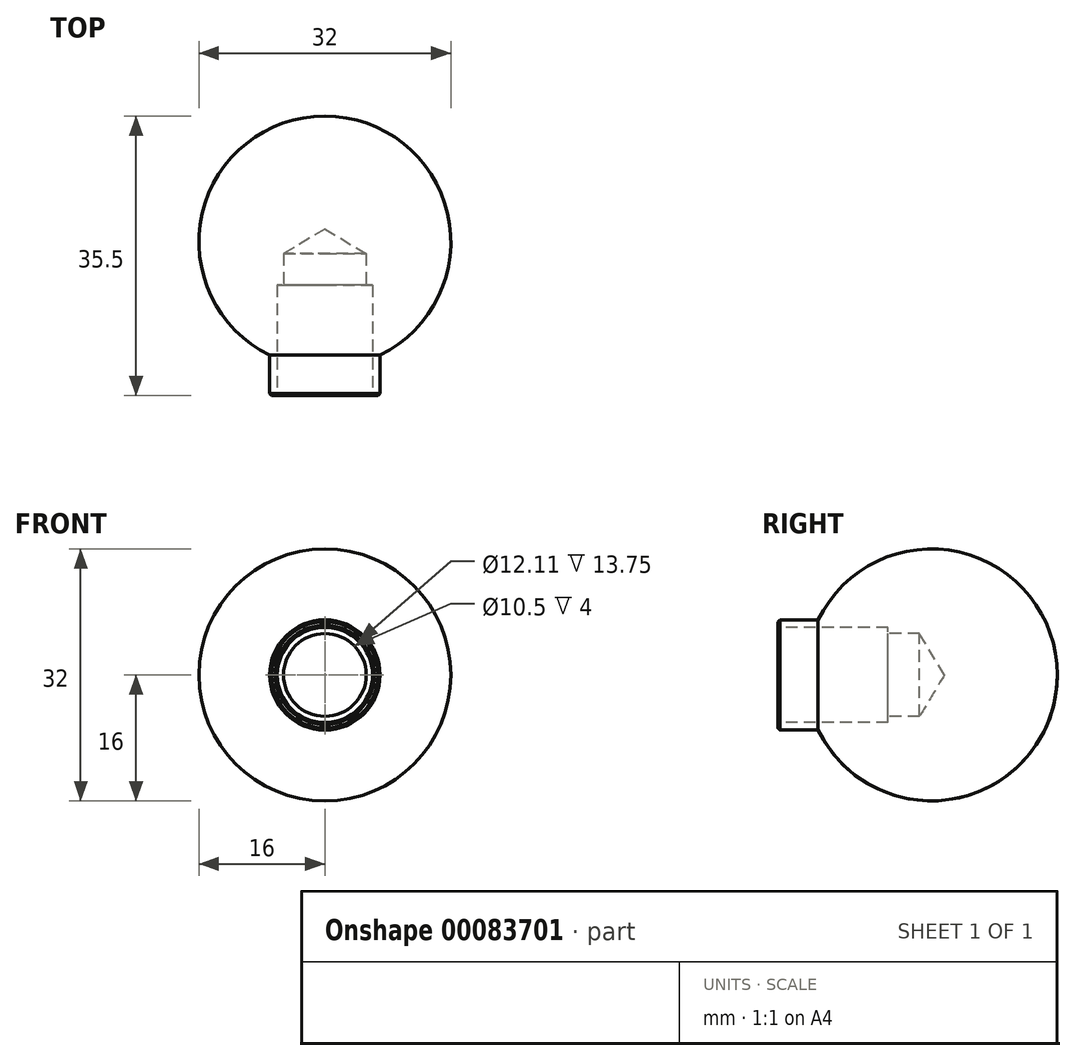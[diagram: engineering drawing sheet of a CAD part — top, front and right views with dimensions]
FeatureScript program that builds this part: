
annotation { "Feature Type Name" : "Feature", "Feature Type Description" : "" }
export const myFeature = defineFeature(function(context is Context, id is Id, definition is map)
    precondition{}
    {
        {
            var Q0;
            Q0=qCreatedBy(makeId("Right.planeOp"),FACE);
            var sketch = newSketch(context, id + "F0", { "sketchPlane" : qUnion([Q0])});
            skArc(sketch, "E0", {"start": v(-14.39, 7) * mm, "mid": v(3.6, 15.6) * mm, "end": v(16, 0) * mm});
            skLineSegment(sketch, "E1", {"start": v(-16, 0) * mm, "end": v(16, 0) * mm});
            skLineSegment(sketch, "E2.left", {"start": v(-16, 0) * mm, "end": v(-16, 0) * mm});
            skLineSegment(sketch, "E3.bottom", {"start": v(-16, 0) * mm, "end": v(-19.5, 0) * mm});
            skLineSegment(sketch, "E3.top", {"start": v(-16, 7) * mm, "end": v(-19.5, 7) * mm});
            skLineSegment(sketch, "E3.right", {"start": v(-19.5, 0) * mm, "end": v(-19.5, 7) * mm});
            skLineSegment(sketch, "E4", {"start": v(-16, 7) * mm, "end": v(-14.39, 7) * mm});
            skSolve(sketch);
        }
        {
            var Q0;
            Q0=qSketchRegion(id+"F0",true);
            var Q1;
            Q1=sQuery(id+"F0.wireOp",EDGE,"E1");
            revolve(context, id + "F1", {"entities" : qUnion([Q0]), "axis" : qUnion([Q1]), "revolveType" : RevolveType.FULL});
        }
        {
            var Q0;
            Q0=makeQuery(id+"F1.opRevolve","SWEPT_FACE",FACE,{"disambiguationData":[OSD([sQuery(id+"F0.wireOp",EDGE,"E3.right")])]});
            var sketch = newSketch(context, id + "F2", { "sketchPlane" : qUnion([Q0])});
            skPoint(sketch, "E5", {"position": v(0, 0) * mm});
            skSolve(sketch);
        }
        {
            var Q0;
            Q0=sQuery(id+"F2.wireOp",VERTEX,"E5");
            var Q1;
            Q1=makeQuery(id+"F1.opRevolve","SWEPT_BODY",BODY,{"disambiguationData":[OSD([sQuery(id+"F0.wireOp",EDGE,"E0"),sQuery(id+"F0.wireOp",EDGE,"E1"),sQuery(id+"F0.wireOp",EDGE,"E3.bottom"),sQuery(id+"F0.wireOp",EDGE,"E3.top"),sQuery(id+"F0.wireOp",EDGE,"E3.right"),sQuery(id+"F0.wireOp",EDGE,"E4")])]});
            hole(context, id + "F3", {"style" : HoleStyle.SIMPLE, "holeDiameter" : 10.5 * mm, "endStyle" : HoleEndStyle.BLIND, "holeDepth" : 18 * mm, "locations" : qUnion([Q0]), "scope" : qUnion([Q1])});
        }
        {
            var Q0;
            Q0=makeQuery(id+"F2.imprint","IMPRINT",FACE,{"disambiguationData":[TD([[makeQuery(id+"F2.imprint","IMPRINT",EDGE,{"derivedFrom":makeQuery(id+"F1.opRevolve","SWEPT_EDGE",EDGE,{"disambiguationData":[OSD([sQuery(id+"F0.wireOp",EDGE,"E3.top"),sQuery(id+"F0.wireOp",EDGE,"E3.right")])]})}),1.0]])]});
            var sketch = newSketch(context, id + "F4", { "sketchPlane" : qUnion([Q0])});
            skCircle(sketch, "E6", {"center": v(0, 0) * mm, "radius": 6.05 * mm});
            skSolve(sketch);
        }
        {
            var Q0;
            Q0=makeQuery(id+"F4.imprint","IMPRINT",FACE,{"disambiguationData":[TD([[makeQuery(id+"F4.imprint","IMPRINT",EDGE,{"derivedFrom":sQuery(id+"F4.wireOp",EDGE,"E6")}),1.0]])]});
            extrude(context, id + "F5", {"entities" : qUnion([Q0]), "operationType" : NewBodyOperationType.REMOVE, "oppositeDirection" : true, "depth" : 14 * mm});
        }
        {
            var Q0;
            Q0=makeQuery(id+"F1.opRevolve","SWEPT_FACE",FACE,{"disambiguationData":[OSD([sQuery(id+"F0.wireOp",EDGE,"E3.right")])]});
            chamfer(context, id + "F6", {"entities" : qUnion([Q0]), "width" : .25 * mm, "tangentPropagation" : true});
        }
    });
